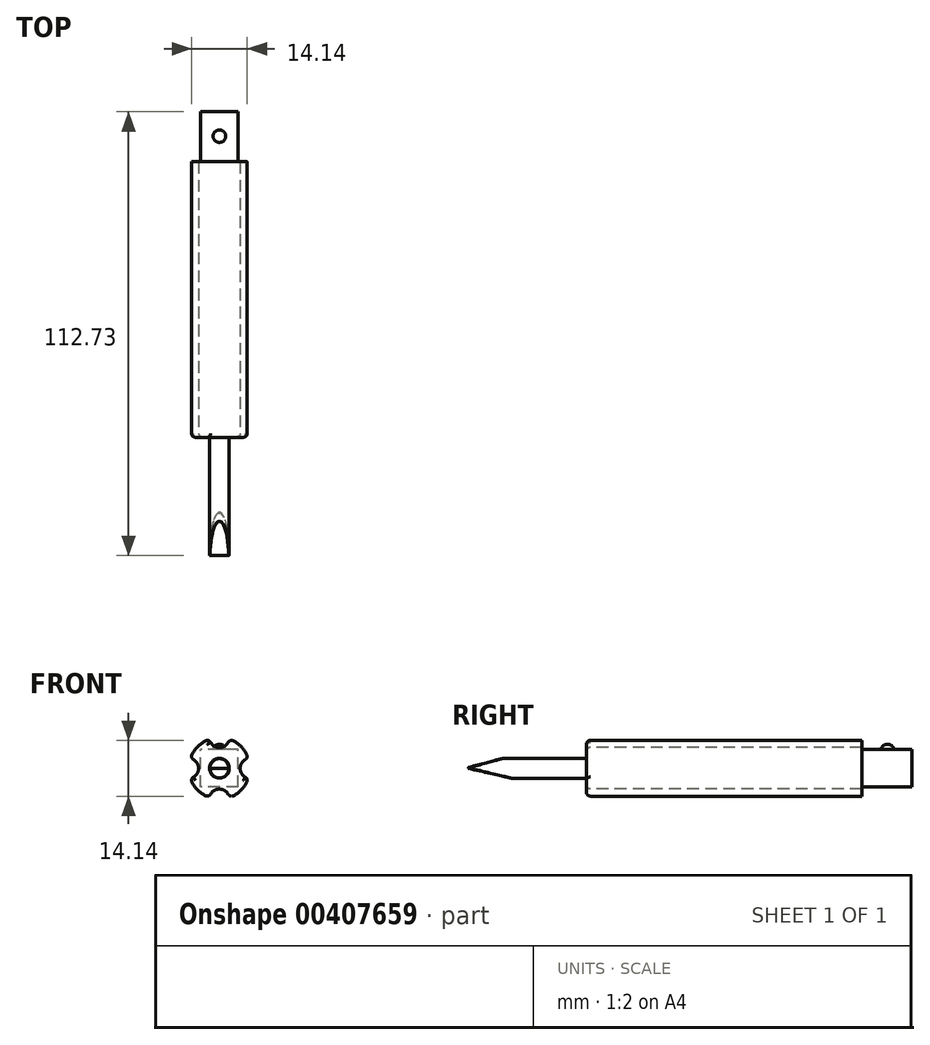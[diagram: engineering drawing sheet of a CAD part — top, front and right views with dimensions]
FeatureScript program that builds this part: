
annotation { "Feature Type Name" : "Feature", "Feature Type Description" : "" }
export const myFeature = defineFeature(function(context is Context, id is Id, definition is map)
    precondition{}
    {
        {
            var Q0;
            Q0=qCreatedBy(makeId("Front.planeOp"),FACE);
            var sketch = newSketch(context, id + "F0", { "sketchPlane" : qUnion([Q0])});
            skCircle(sketch, "E0", {"center": v(0, 0) * mm, "radius": 7.81 * mm});
            skSolve(sketch);
        }
        {
            var Q0;
            Q0 = qSketchRegion(id + "F0", true);
            extrude(context, id + "F1", {"entities" : qUnion([Q0]), "endBound" : BoundingType.SYMMETRIC, "depth" : 70 * mm});
        }
        {
            var Q0;
            Q0=qCreatedBy(makeId("Front.planeOp"),FACE);
            var sketch = newSketch(context, id + "F2", { "sketchPlane" : qUnion([Q0])});
            skCircle(sketch, "E1", {"center": v(0, 7.81) * mm, "radius": 2.54 * mm});
            skCircle(sketch, "E2", {"center": v(7.81, 0) * mm, "radius": 2.54 * mm});
            skCircle(sketch, "E3", {"center": v(0, -7.81) * mm, "radius": 2.54 * mm});
            skCircle(sketch, "E4", {"center": v(-7.82, 0) * mm, "radius": 2.54 * mm});
            skSolve(sketch);
        }
        {
            var Q0;
            Q0=makeQuery(id+"F2.imprint","IMPRINT",FACE,{"disambiguationData":[TD([[makeQuery(id+"F2.imprint","IMPRINT",EDGE,{"derivedFrom":sQuery(id+"F2.wireOp",EDGE,"E1")}),1.0]])]});
            var Q1;
            Q1=makeQuery(id+"F2.imprint","IMPRINT",FACE,{"disambiguationData":[TD([[makeQuery(id+"F2.imprint","IMPRINT",EDGE,{"derivedFrom":sQuery(id+"F2.wireOp",EDGE,"E4")}),1.0]])]});
            var Q2;
            Q2=makeQuery(id+"F2.imprint","IMPRINT",FACE,{"disambiguationData":[TD([[makeQuery(id+"F2.imprint","IMPRINT",EDGE,{"derivedFrom":sQuery(id+"F2.wireOp",EDGE,"E3")}),1.0]])]});
            var Q3;
            Q3=makeQuery(id+"F2.imprint","IMPRINT",FACE,{"disambiguationData":[TD([[makeQuery(id+"F2.imprint","IMPRINT",EDGE,{"derivedFrom":sQuery(id+"F2.wireOp",EDGE,"E2")}),1.0]])]});
            extrude(context, id + "F3", {"entities" : qUnion([Q0, Q1, Q2, Q3]), "operationType" : NewBodyOperationType.REMOVE, "endBound" : BoundingType.SYMMETRIC, "oppositeDirection" : true, "depth" : 70 * mm});
        }
        {
            var Q0;
            Q0=makeQuery(id+"F1.opExtrude","CAP_FACE",FACE,{"disambiguationData":[OSD([sQuery(id+"F0.wireOp",EDGE,"E0")])],"isStart":false});
            var Q1;
            Q1=makeQuery(id+"F3.boolean.opBoolean","INTERSECT",EDGE,{"disambiguationData":[OD(1.0)],"derivedFrom":[makeQuery(id+"F1.opExtrude","SWEPT_FACE",FACE,{"disambiguationData":[OSD([sQuery(id+"F0.wireOp",EDGE,"E0")])]}),makeQuery(id+"F3.opExtrude","SWEPT_FACE",FACE,{"disambiguationData":[OSD([sQuery(id+"F2.wireOp",EDGE,"E2")])]})]});
            var Q2;
            Q2=makeQuery(id+"F3.boolean.opBoolean","INTERSECT",EDGE,{"disambiguationData":[OD(0.0)],"derivedFrom":[makeQuery(id+"F1.opExtrude","SWEPT_FACE",FACE,{"disambiguationData":[OSD([sQuery(id+"F0.wireOp",EDGE,"E0")])]}),makeQuery(id+"F3.opExtrude","SWEPT_FACE",FACE,{"disambiguationData":[OSD([sQuery(id+"F2.wireOp",EDGE,"E2")])]})]});
            var Q3;
            Q3=makeQuery(id+"F3.boolean.opBoolean","INTERSECT",EDGE,{"disambiguationData":[OD(0.0)],"derivedFrom":[makeQuery(id+"F1.opExtrude","SWEPT_FACE",FACE,{"disambiguationData":[OSD([sQuery(id+"F0.wireOp",EDGE,"E0")])]}),makeQuery(id+"F3.opExtrude","SWEPT_FACE",FACE,{"disambiguationData":[OSD([sQuery(id+"F2.wireOp",EDGE,"E1")])]})]});
            var Q4;
            Q4=makeQuery(id+"F3.boolean.opBoolean","INTERSECT",EDGE,{"disambiguationData":[OD(1.0)],"derivedFrom":[makeQuery(id+"F1.opExtrude","SWEPT_FACE",FACE,{"disambiguationData":[OSD([sQuery(id+"F0.wireOp",EDGE,"E0")])]}),makeQuery(id+"F3.opExtrude","SWEPT_FACE",FACE,{"disambiguationData":[OSD([sQuery(id+"F2.wireOp",EDGE,"E1")])]})]});
            var Q5;
            Q5=makeQuery(id+"F3.boolean.opBoolean","INTERSECT",EDGE,{"disambiguationData":[OD(0.0)],"derivedFrom":[makeQuery(id+"F1.opExtrude","SWEPT_FACE",FACE,{"disambiguationData":[OSD([sQuery(id+"F0.wireOp",EDGE,"E0")])]}),makeQuery(id+"F3.opExtrude","SWEPT_FACE",FACE,{"disambiguationData":[OSD([sQuery(id+"F2.wireOp",EDGE,"E4")])]})]});
            var Q6;
            Q6=makeQuery(id+"F3.boolean.opBoolean","INTERSECT",EDGE,{"disambiguationData":[OD(1.0)],"derivedFrom":[makeQuery(id+"F1.opExtrude","SWEPT_FACE",FACE,{"disambiguationData":[OSD([sQuery(id+"F0.wireOp",EDGE,"E0")])]}),makeQuery(id+"F3.opExtrude","SWEPT_FACE",FACE,{"disambiguationData":[OSD([sQuery(id+"F2.wireOp",EDGE,"E4")])]})]});
            var Q7;
            Q7=makeQuery(id+"F3.boolean.opBoolean","INTERSECT",EDGE,{"disambiguationData":[OD(1.0)],"derivedFrom":[makeQuery(id+"F1.opExtrude","SWEPT_FACE",FACE,{"disambiguationData":[OSD([sQuery(id+"F0.wireOp",EDGE,"E0")])]}),makeQuery(id+"F3.opExtrude","SWEPT_FACE",FACE,{"disambiguationData":[OSD([sQuery(id+"F2.wireOp",EDGE,"E3")])]})]});
            var Q8;
            Q8=makeQuery(id+"F3.boolean.opBoolean","INTERSECT",EDGE,{"disambiguationData":[OD(0.0)],"derivedFrom":[makeQuery(id+"F1.opExtrude","SWEPT_FACE",FACE,{"disambiguationData":[OSD([sQuery(id+"F0.wireOp",EDGE,"E0")])]}),makeQuery(id+"F3.opExtrude","SWEPT_FACE",FACE,{"disambiguationData":[OSD([sQuery(id+"F2.wireOp",EDGE,"E3")])]})]});
            fillet(context, id + "F4", {"entities" : qUnion([Q0, Q1, Q2, Q3, Q4, Q5, Q6, Q7, Q8]), "radius" : 1 * mm, "tangentPropagation" : true, "allowEdgeOverflow" : false});
        }
        {
            var Q0;
            Q0=makeQuery(id+"F1.opExtrude","CAP_FACE",FACE,{"disambiguationData":[OSD([sQuery(id+"F0.wireOp",EDGE,"E0")])],"isStart":false});
            var sketch = newSketch(context, id + "F5", { "sketchPlane" : qUnion([Q0])});
            skCircle(sketch, "E5", {"center": v(0, 0) * mm, "radius": 2.5 * mm});
            skSolve(sketch);
        }
        {
            var Q0;
            Q0 = qSketchRegion(id + "F5", true);
            extrude(context, id + "F6", {"entities" : qUnion([Q0]), "operationType" : NewBodyOperationType.ADD, "depth" : 30 * mm});
        }
        {
            var Q0;
            Q0=qCreatedBy(makeId("Right.planeOp"),FACE);
            var sketch = newSketch(context, id + "F7", { "sketchPlane" : qUnion([Q0])});
            skLineSegment(sketch, "E6", {"start": v(-65.03, 0) * mm, "end": v(-52.92, -2.76) * mm});
            skLineSegment(sketch, "E7", {"start": v(-52.92, -2.76) * mm, "end": v(-65.64, -2.76) * mm});
            skLineSegment(sketch, "E8", {"start": v(-65.64, -2.76) * mm, "end": v(-65.64, 3.4) * mm});
            skLineSegment(sketch, "E9", {"start": v(-65.64, 3.4) * mm, "end": v(-52.92, 3.4) * mm});
            skLineSegment(sketch, "E10", {"start": v(-52.92, 3.4) * mm, "end": v(-65.03, 0.2) * mm});
            skLineSegment(sketch, "E11", {"start": v(-65.03, 0.2) * mm, "end": v(-65.03, 0) * mm});
            skSolve(sketch);
        }
        {
            var Q0;
            Q0 = qSketchRegion(id + "F7", true);
            extrude(context, id + "F8", {"entities" : qUnion([Q0]), "operationType" : NewBodyOperationType.REMOVE, "endBound" : BoundingType.SYMMETRIC, "oppositeDirection" : true, "depth" : 25.4 * mm});
        }
        {
            var Q0;
            Q0=makeQuery(id+"F8.boolean.opBoolean","COPY",FACE,{"derivedFrom":makeQuery(id+"F8.opExtrude","SWEPT_FACE",FACE,{"disambiguationData":[OSD([sQuery(id+"F7.wireOp",EDGE,"E10")])]})});
            var Q1;
            Q1=makeQuery(id+"F8.boolean.opBoolean","INTERSECT",EDGE,{"derivedFrom":[makeQuery(id+"F6.opExtrude","SWEPT_FACE",FACE,{"disambiguationData":[OSD([sQuery(id+"F5.wireOp",EDGE,"E5")])]}),makeQuery(id+"F8.opExtrude","SWEPT_FACE",FACE,{"disambiguationData":[OSD([sQuery(id+"F7.wireOp",EDGE,"E6")])]})]});
            fillet(context, id + "F9", {"entities" : qUnion([Q0, Q1]), "radius" : 0.13 * mm, "tangentPropagation" : true, "allowEdgeOverflow" : false});
        }
        {
            var Q0;
            Q0=makeQuery(id+"F1.opExtrude","CAP_FACE",FACE,{"disambiguationData":[OSD([sQuery(id+"F0.wireOp",EDGE,"E0")])],"isStart":true});
            var sketch = newSketch(context, id + "F10", { "sketchPlane" : qUnion([Q0])});
            skLineSegment(sketch, "E12.bottom", {"start": v(-4.76, -4.76) * mm, "end": v(4.76, -4.76) * mm});
            skLineSegment(sketch, "E12.top", {"start": v(-4.76, 4.76) * mm, "end": v(4.76, 4.76) * mm});
            skLineSegment(sketch, "E12.left", {"start": v(-4.76, -4.76) * mm, "end": v(-4.76, 4.76) * mm});
            skLineSegment(sketch, "E12.right", {"start": v(4.76, -4.76) * mm, "end": v(4.76, 4.76) * mm});
            skPoint(sketch, "E12.middle", {"position": v(0, 0) * mm});
            skSolve(sketch);
        }
        {
            var Q0;
            Q0=makeQuery(id+"F10.imprint","IMPRINT",FACE,{"disambiguationData":[TD([[makeQuery(id+"F10.imprint","IMPRINT",EDGE,{"derivedFrom":sQuery(id+"F10.wireOp",EDGE,"E12.bottom")}),1.0]])]});
            extrude(context, id + "F11", {"entities" : qUnion([Q0]), "operationType" : NewBodyOperationType.ADD, "depth" : 12.7 * mm});
        }
        {
            var Q0;
            Q0=makeQuery(id+"F11.opExtrude","SWEPT_FACE",FACE,{"disambiguationData":[OSD([sQuery(id+"F10.wireOp",EDGE,"E12.top")])]});
            var sketch = newSketch(context, id + "F12", { "sketchPlane" : qUnion([Q0])});
            skCircle(sketch, "E13", {"center": v(0, 41.5) * mm, "radius": 1.59 * mm});
            skPoint(sketch, "E13.centerSnap0", {"position": v(0, 47.7) * mm});
            skSolve(sketch);
        }
        {
            var Q0;
            Q0 = qSketchRegion(id + "F12", true);
            extrude(context, id + "F13", {"entities" : qUnion([Q0]), "operationType" : NewBodyOperationType.ADD, "depth" : 1.27 * mm});
        }
        {
            var Q0;
            Q0=makeQuery(id+"F13.opExtrude","CAP_EDGE",EDGE,{"disambiguationData":[OSD([sQuery(id+"F12.wireOp",EDGE,"E13")])],"isStart":false});
            fillet(context, id + "F14", {"entities" : qUnion([Q0]), "radius" : 1.27 * mm, "tangentPropagation" : true, "allowEdgeOverflow" : false});
        }
    });
